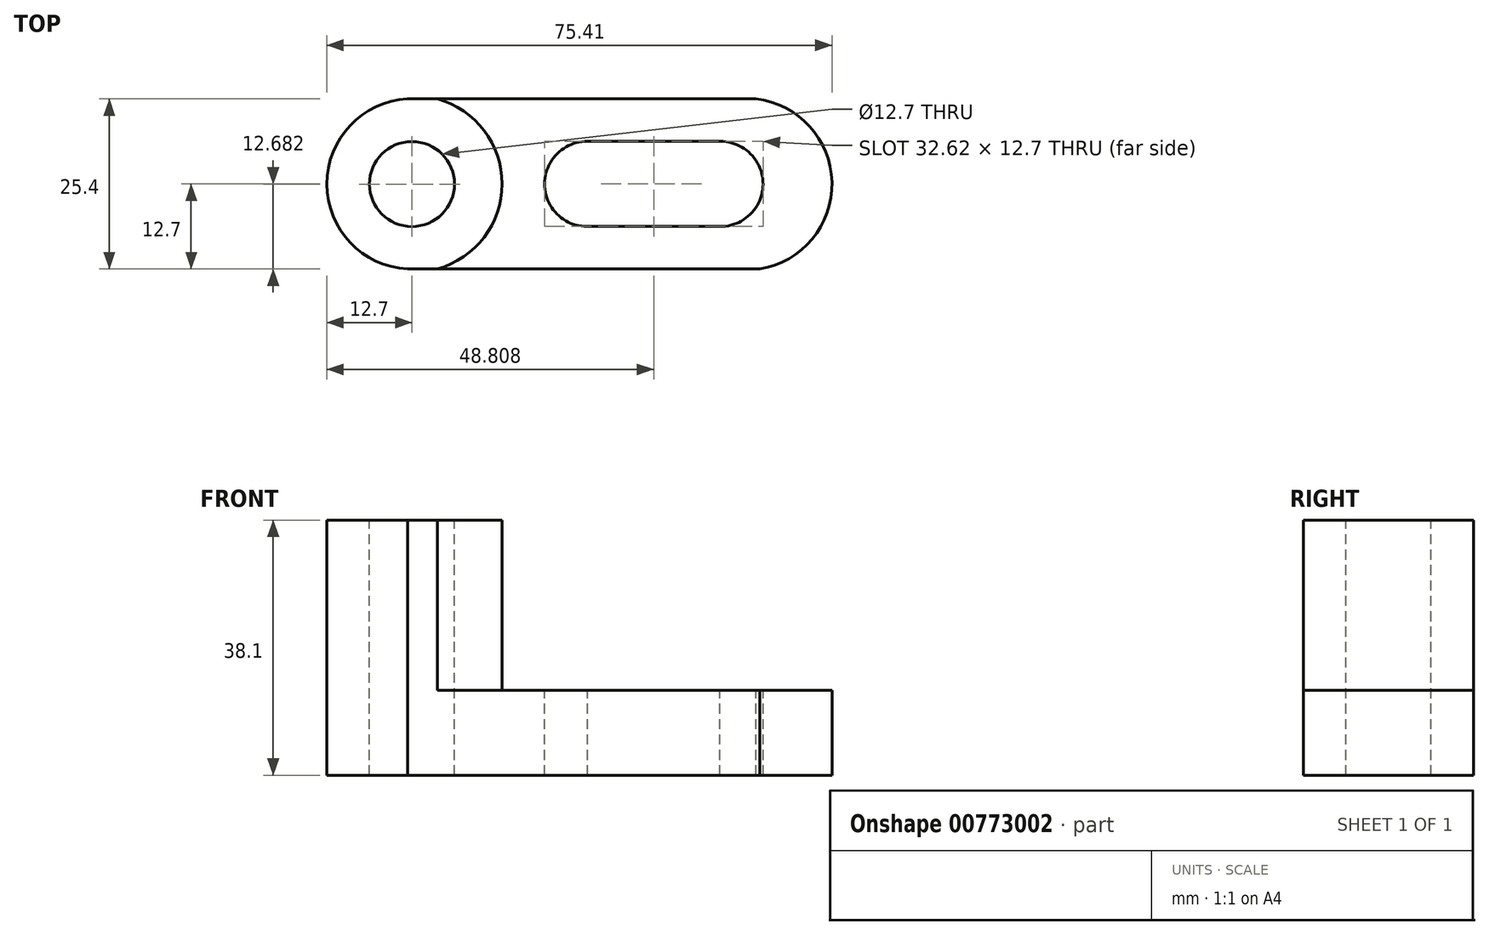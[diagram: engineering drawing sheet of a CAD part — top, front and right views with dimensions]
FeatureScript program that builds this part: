
annotation { "Feature Type Name" : "Feature", "Feature Type Description" : "" }
export const myFeature = defineFeature(function(context is Context, id is Id, definition is map)
    precondition{}
    {
        {
            var Q0;
            Q0=qCreatedBy(makeId("Front.planeOp"),FACE);
            var sketch = newSketch(context, id + "F0", { "sketchPlane" : qUnion([Q0])});
            skLineSegment(sketch, "E0", {"start": v(0, 0) * mm, "end": v(76.2, 0) * mm});
            skLineSegment(sketch, "E1", {"start": v(76.2, 0) * mm, "end": v(76.2, 12.7) * mm});
            skLineSegment(sketch, "E2", {"start": v(76.2, 12.7) * mm, "end": v(0, 12.7) * mm});
            skLineSegment(sketch, "E3", {"start": v(0, 12.7) * mm, "end": v(0, 0) * mm});
            skSolve(sketch);
        }
        {
            var Q0;
            Q0=makeQuery(id+"F0.imprint","IMPRINT",FACE,{"disambiguationData":[TD([[makeQuery(id+"F0.imprint","IMPRINT",EDGE,{"derivedFrom":sQuery(id+"F0.wireOp",EDGE,"E0")}),1.0]])]});
            extrude(context, id + "F1", {"entities" : qUnion([Q0]), "depth" : 25.4 * mm, "offsetDistance" : 25.4 * mm});
        }
        {
            var Q0;
            Q0=makeQuery(id+"F1.opExtrude","SWEPT_FACE",FACE,{"disambiguationData":[OSD([sQuery(id+"F0.wireOp",EDGE,"E2")])]});
            var sketch = newSketch(context, id + "F2", { "sketchPlane" : qUnion([Q0])});
            skArc(sketch, "E4", {"start": v(64.66, -25.4) * mm, "mid": v(75.4, -12.43) * mm, "end": v(64.04, 0) * mm});
            skSolve(sketch);
        }
        {
            var Q0;
            {var subQ0=sQuery(id+"F2.wireOp",EDGE,"E4");Q0=makeQuery(id+"F2.imprint","IMPRINT",FACE,{"disambiguationData":[TD([[makeQuery(id+"F2.imprint","IMPRINT",EDGE,{"derivedFrom":subQ0}),-1.0]])]});}
            extrude(context, id + "F3", {"entities" : qUnion([Q0]), "operationType" : NewBodyOperationType.REMOVE, "oppositeDirection" : true, "depth" : 25.4 * mm, "offsetDistance" : 25.4 * mm});
        }
        {
            var Q0;
            Q0=makeQuery(id+"F1.opExtrude","SWEPT_FACE",FACE,{"disambiguationData":[OSD([sQuery(id+"F0.wireOp",EDGE,"E2")])]});
            var sketch = newSketch(context, id + "F4", { "sketchPlane" : qUnion([Q0])});
            skCircle(sketch, "E5", {"center": v(12.7, -12.72) * mm, "radius": 12.7 * mm});
            skCircle(sketch, "E6", {"center": v(12.7, -12.72) * mm, "radius": 6.35 * mm});
            skSolve(sketch);
        }
        {
            var Q0;
            {var subQ0=sQuery(id+"F4.wireOp",EDGE,"E5");var subQ1=sQuery(id+"F0.wireOp",EDGE,"E2");var subQ2=makeQuery(id+"F1.opExtrude","SWEPT_EDGE",EDGE,{"disambiguationData":[OSD([subQ1,sQuery(id+"F0.wireOp",EDGE,"E3")])]});var subQ3=makeQuery(id+"F4.imprint","INTERSECT",VERTEX,{"disambiguationData":[OD(0.0)],"derivedFrom":[subQ2,subQ0]});var subQ4=makeQuery(id+"F1.opExtrude","CAP_EDGE",EDGE,{"disambiguationData":[OSD([subQ1])],"isStart":false});var subQ5=makeQuery(id+"F4.imprint","INTERSECT",VERTEX,{"disambiguationData":[OD(0.0)],"derivedFrom":[subQ4,subQ0]});Q0=makeQuery(id+"F4.imprint","IMPRINT",FACE,{"disambiguationData":[TD([[makeQuery(id+"F4.imprint","IMPRINT",EDGE,{"disambiguationData":[TD([[subQ3,-1.0],[subQ5,1.0]])],"derivedFrom":subQ0}),-1.0]])]});}
            var Q1;
            Q1=makeQuery(id+"F4.imprint","IMPRINT",FACE,{"disambiguationData":[TD([[makeQuery(id+"F4.imprint","IMPRINT",EDGE,{"derivedFrom":sQuery(id+"F4.wireOp",EDGE,"E6")}),1.0]])]});
            extrude(context, id + "F5", {"entities" : qUnion([Q0, Q1]), "operationType" : NewBodyOperationType.REMOVE, "oppositeDirection" : true, "depth" : 50.8 * mm, "offsetDistance" : 25.4 * mm});
        }
        {
            var Q0;
            Q0=makeQuery(id+"F1.opExtrude","SWEPT_FACE",FACE,{"disambiguationData":[OSD([sQuery(id+"F0.wireOp",EDGE,"E2")])]});
            var sketch = newSketch(context, id + "F6", { "sketchPlane" : qUnion([Q0])});
            skArc(sketch, "E7", {"start": v(13.5, 0) * mm, "mid": v(4, -3.45) * mm, "end": v(0, -12.74) * mm});
            skSolve(sketch);
        }
        {
            var Q0;
            {var subQ1=sQuery(id+"F0.wireOp",EDGE,"E2");var subQ2=makeQuery(id+"F1.opExtrude","SWEPT_EDGE",EDGE,{"disambiguationData":[OSD([subQ1,sQuery(id+"F0.wireOp",EDGE,"E3")])]});Q0=makeQuery(id+"F6.imprint","IMPRINT",FACE,{"disambiguationData":[TD([[makeQuery(id+"F6.imprint","IMPRINT",EDGE,{"derivedFrom":subQ2}),-1.0]])]});}
            extrude(context, id + "F7", {"entities" : qUnion([Q0]), "operationType" : NewBodyOperationType.REMOVE, "oppositeDirection" : true, "depth" : 25.4 * mm, "offsetDistance" : 25.4 * mm});
        }
        {
            var Q0;
            Q0=makeQuery(id+"F1.opExtrude","SWEPT_FACE",FACE,{"disambiguationData":[OSD([sQuery(id+"F0.wireOp",EDGE,"E2")])]});
            var sketch = newSketch(context, id + "F8", { "sketchPlane" : qUnion([Q0])});
            skArc(sketch, "E8", {"start": v(16.52, -25.4) * mm, "mid": v(26.15, -12.7) * mm, "end": v(16.52, 0) * mm});
            skSolve(sketch);
        }
        {
            var Q0;
            Q0=makeQuery(id+"F1.opExtrude","SWEPT_FACE",FACE,{"disambiguationData":[OSD([sQuery(id+"F0.wireOp",EDGE,"E2")])]});
            var sketch = newSketch(context, id + "F9", { "sketchPlane" : qUnion([Q0])});
            skCircle(sketch, "E9", {"center": v(38.85, -12.7) * mm, "radius": 6.35 * mm});
            skCircle(sketch, "E10", {"center": v(58.77, -12.7) * mm, "radius": 6.35 * mm});
            skLineSegment(sketch, "E11", {"start": v(38.79, -6.35) * mm, "end": v(58.77, -6.35) * mm});
            skLineSegment(sketch, "E12", {"start": v(58.87, -19.05) * mm, "end": v(38.85, -19.05) * mm});
            skSolve(sketch);
        }
        {
            var Q0;
            {var subQ2=sQuery(id+"F8.wireOp",EDGE,"E8");Q0=makeQuery(id+"F8.imprint","IMPRINT",FACE,{"disambiguationData":[TD([[makeQuery(id+"F8.imprint","IMPRINT",EDGE,{"derivedFrom":subQ2}),1.0]])]});}
            extrude(context, id + "F10", {"entities" : qUnion([Q0]), "operationType" : NewBodyOperationType.ADD, "depth" : 25.4 * mm, "offsetDistance" : 25.4 * mm});
        }
        {
            var Q0;
            Q0=makeQuery(id+"F9.imprint","IMPRINT",FACE,{"disambiguationData":[TD([[makeQuery(id+"F9.imprint","IMPRINT",EDGE,{"derivedFrom":sQuery(id+"F9.wireOp",EDGE,"E9")}),-1.0]])]});
            var sketch = newSketch(context, id + "F11", { "sketchPlane" : qUnion([Q0])});
            skLineSegment(sketch, "E13", {"start": v(58.85, -6.25) * mm, "end": v(38.67, -6.25) * mm});
            skLineSegment(sketch, "E14", {"start": v(58.87, -19.05) * mm, "end": v(38.4, -19.05) * mm});
            skSolve(sketch);
        }
        {
            var Q0;
            {var subQ0=sQuery(id+"F11.wireOp",EDGE,"E14");var subQ1=makeQuery(id+"F9.imprint","IMPRINT",EDGE,{"derivedFrom":sQuery(id+"F9.wireOp",EDGE,"E9")});var subQ2=makeQuery(id+"F11.imprint","INTERSECT",VERTEX,{"disambiguationData":[OD(0.0)],"derivedFrom":[subQ1,subQ0]});Q0=makeQuery(id+"F11.imprint","IMPRINT",FACE,{"disambiguationData":[TD([[makeQuery(id+"F11.imprint","IMPRINT",EDGE,{"disambiguationData":[TD([[subQ2,1.0]])],"derivedFrom":subQ0}),-1.0]])]});}
            var Q1;
            Q1=makeQuery(id+"F11.imprint","IMPRINT",FACE,{"disambiguationData":[TD([[makeQuery(id+"F11.imprint","IMPRINT",EDGE,{"derivedFrom":makeQuery(id+"F9.imprint","IMPRINT",EDGE,{"derivedFrom":sQuery(id+"F9.wireOp",EDGE,"E10")})}),1.0]])]});
            extrude(context, id + "F12", {"entities" : qUnion([Q0, Q1]), "operationType" : NewBodyOperationType.REMOVE, "oppositeDirection" : true, "depth" : 25.4 * mm, "offsetDistance" : 25.4 * mm});
        }
        {
            var Q0;
            {var subQ0=sQuery(id+"F9.wireOp",EDGE,"E9");var subQ2=makeQuery(id+"F9.imprint","IMPRINT",VERTEX,{"derivedFrom":subQ0});Q0=makeQuery(id+"F9.imprint","IMPRINT",FACE,{"disambiguationData":[TD([[makeQuery(id+"F9.imprint","IMPRINT",EDGE,{"disambiguationData":[TD([[subQ2,1.0]])],"derivedFrom":subQ0}),1.0]])]});}
            var Q1;
            {var subQ0=sQuery(id+"F9.wireOp",EDGE,"E11");Q1=makeQuery(id+"F9.imprint","IMPRINT",FACE,{"disambiguationData":[TD([[makeQuery(id+"F9.imprint","IMPRINT",EDGE,{"derivedFrom":subQ0}),-1.0]])]});}
            var Q2;
            {var subQ0=sQuery(id+"F9.wireOp",EDGE,"E10");var subQ1=makeQuery(id+"F9.imprint","INTERSECT",VERTEX,{"derivedFrom":[subQ0,sQuery(id+"F9.wireOp",EDGE,"E11")]});Q2=makeQuery(id+"F9.imprint","IMPRINT",FACE,{"disambiguationData":[TD([[makeQuery(id+"F9.imprint","IMPRINT",EDGE,{"disambiguationData":[TD([[subQ1,-1.0]])],"derivedFrom":subQ0}),1.0]])]});}
            extrude(context, id + "F13", {"entities" : qUnion([Q0, Q1, Q2]), "operationType" : NewBodyOperationType.REMOVE, "oppositeDirection" : true, "depth" : 25.4 * mm, "offsetDistance" : 25.4 * mm});
        }
    });
